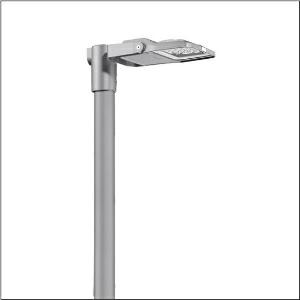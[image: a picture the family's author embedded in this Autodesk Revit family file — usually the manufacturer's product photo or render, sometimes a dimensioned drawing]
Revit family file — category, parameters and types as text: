
# Revit family: floodlight_fl_21_iq_micro___pl64_5xa7761a4e3a_8e2d
name_source: partatom
category: Lighting Fixtures
units: mm (PartAtom-declared; Revit-internal decimal feet)

## family parameters
Cut with Voids When Loaded = No
Host = Face
Light Source = No
Part Type = Normal
Room Calculation Point = No
Round Connector Dimension = Use Diameter
Shared = No

## types (1)
- --- (1 x LED, 2980 lm, 23.1 W, 4000K)
    Apparent Load = 23 VA
    CIE Flux Codes = 28 80 98 100 100
    Color Rendering = 70
    Color Temperature = 4000K
    Default Elevation = 1800 mm
    Description = Floodlight FL 21 iQ micro, floodlight, primary light control with lens, of PMMA, primary optical cover: protective disc, of toughened safety glass, transparent, light distribution: PL64, light emission: direct distribution, installation type: surface-mounted, LED, High Power LED, rated luminous flux: 2.980lm, luminous efficacy: 129lm/W, light colour: 740, colour temperature: 4000K, control: optimised constant luminous flux control (CLO 2.0), Desk-Remote (wireless, voltage-free reading and setting of iQ features in the workshop via application-optimized NFC function/RFID function), Light-Fading, Smart-Wire, Night-Set, Lumen-Switch, Temp-Guard, Auto-Match, with terminal, 6-pole, mains connection: 220..240V, AC, 50/60Hz, start of lifetime: 23W, end of service life: 24W, reduction: 11W, luminaire housing, of diecast aluminium, powder-coated, Siteco® metallic grey (DB 702S), corrosivity category C5 mid according to DIN EN ISO 12944, sealing non-destructively replaceable, please order mast flange separately, mast bracket, of steel, galvanised, powder-coated, Siteco® metallic grey (DB 702S), protection rating (complete): IP66, insulation class (complete): insulation class II (safety insulation), certification: CE, ENEC, VDE, protection symbol: D, impact resistance: IK07, permissible operating ambient temperature: -40..+40°C, permissible operating ambient temperature for outdoor applications: -40..+50°C, standard: DIN EN 12944, LABS conformity tested according to VDMA 24364:2018-05, packaging unit: 1 piece

Light Distribution: PL64
    Height = 65 mm
    Lamp = 1 x LED
    Lamp Light Flux = 2980 lm
    Lamp Power = 23.1 W
    Lamp count = 1
    Length = 312 mm
    Luminous efficacy = 129 lm/W
    Manufacturer = Siteco
    ModVariant = No
    Model = 5XA7761A4E3A
    Number of Poles = 1
    OnlyDefault = Yes
    Power Factor = 1
    Product Name = Floodlight FL 21 iQ micro | PL64
    Product group = floodlight | pylon annexe
    ProductGroupID = 6200
    Protection Class = Protection class II
    Protection Degree = IP 66
    RLX_Detail_Level = 1
    RLX_Emergency_Light_Flux = 0 lm
    RLX_Emergency_Type = 0
    RLX_Emergency_Type_DB = No
    RlxData = <blob elided: 101897 chars, md5=c7d5d2c5>
    Socket = socket
    Standby Power = 0 W
    System Light Flux = 2980 lm
    System Power = 23 W
    Type Comments = factory setting: luminous flux: 100 % | dim-lin: 254 | 455 mA
    Type Image = l_1007121.jpg
    URL = http://relux.com
    VarID = @adj_113827
    Voltage = 0 V
    Weight = 0.00 kg
    Width = 230 mm

## geometry (parser evidence)
native form markers: Blend x4, Sweep x11
no freeform markers — native parametric forms only
